# Revit family: Power-ModularDevices-GEWISS-90AM-CONTACTORS_40A
name_source: partatom
category: Apparecchi elettrici
revit_build: Autodesk Revit 2016 (Build: 20161004_0715(x64)
units: mm (PartAtom-declared; Revit-internal decimal feet)

## family parameters
Condiviso = No
Host = Superficie
Mantenere orientamento annotazione = Sì
Numero OmniClass = 23.80.30.00
Punto di calcolo locali = Sì
Quota connettore circolare = Usa diametro
Taglio con vuoti quando caricato = No
Tipo di parte = Normale
Titolo OmniClass = Distribution Devices

## types (5) — shared parameters
A = 54 mm  [stored 0.177165 ft]
B = 85 mm  [stored 0.278871 ft]
C = 65 mm  [stored 0.213255 ft]
Catalogue = POWER
Catalogue Range = 90 AM
D = 45 mm  [stored 0.147638 ft]
Electrocod = 1712
Fin_contattore = <Per categoria>
IDF = 1bff8ad1-67a9-48c8-9278-5f77d0eb7883
IDT = cf1be6d4-11a6-4aae-8e9c-46eae0d5676d
Immagine tipo = GWD6725.jpg
No. Chorus modules = 3
Numero poli = 1
Potenza in Watt = 0 V
Produttore = GEWISS S.p.A.
Prospetto di default = 1219 mm
Rated current (AC-1/AC-7a) = 40 A - CTR40
TEXT LABEL = A
Technical sheet = https://www.gewiss.com
URL = https://www.gewiss.com
Version file RFA = 18.0

## per-type parameters (varying)
| type | Control coil voltage (V) | Descrizione | EAN code | Modello |
| GWD6721 - CONTACTOR 40A 2NO 230V 3M | 230Vac - 220Vdc | CONTACTOR 40A 2NO 230V 3M | 8011564809598 | GWD6721 |
| GWD6724 - CONTACTOR 40A 4NO 230V 3M | 230Vac - 220Vdc | CONTACTOR 40A 4NO 230V 3M | 8011564809611 | GWD6724 |
| GWD6725 - CONTACTOR 40A 2NO+2NC 230V 3M | 230Vac - 220Vdc | CONTACTOR 40A 2NO+2NC 230V 3M | 8011564809628 | GWD6725 |
| GWD6722 - CONTACTOR 40A 3NO 230V 3M | 230Vac - 220Vdc | CONTACTOR 40A 3NO 230V 3M | 8011564809581 | GWD6722 |
| GWD6723 - CONTACTOR 40A 4NO 24V 3M | 24Vac/dc | CONTACTOR 40A 4NO 24V 3M | 8011564809604 | GWD6723 |

note: [stored X ft] marks values corroborated as IEEE doubles in the binary element streams (Revit-internal decimal feet)
